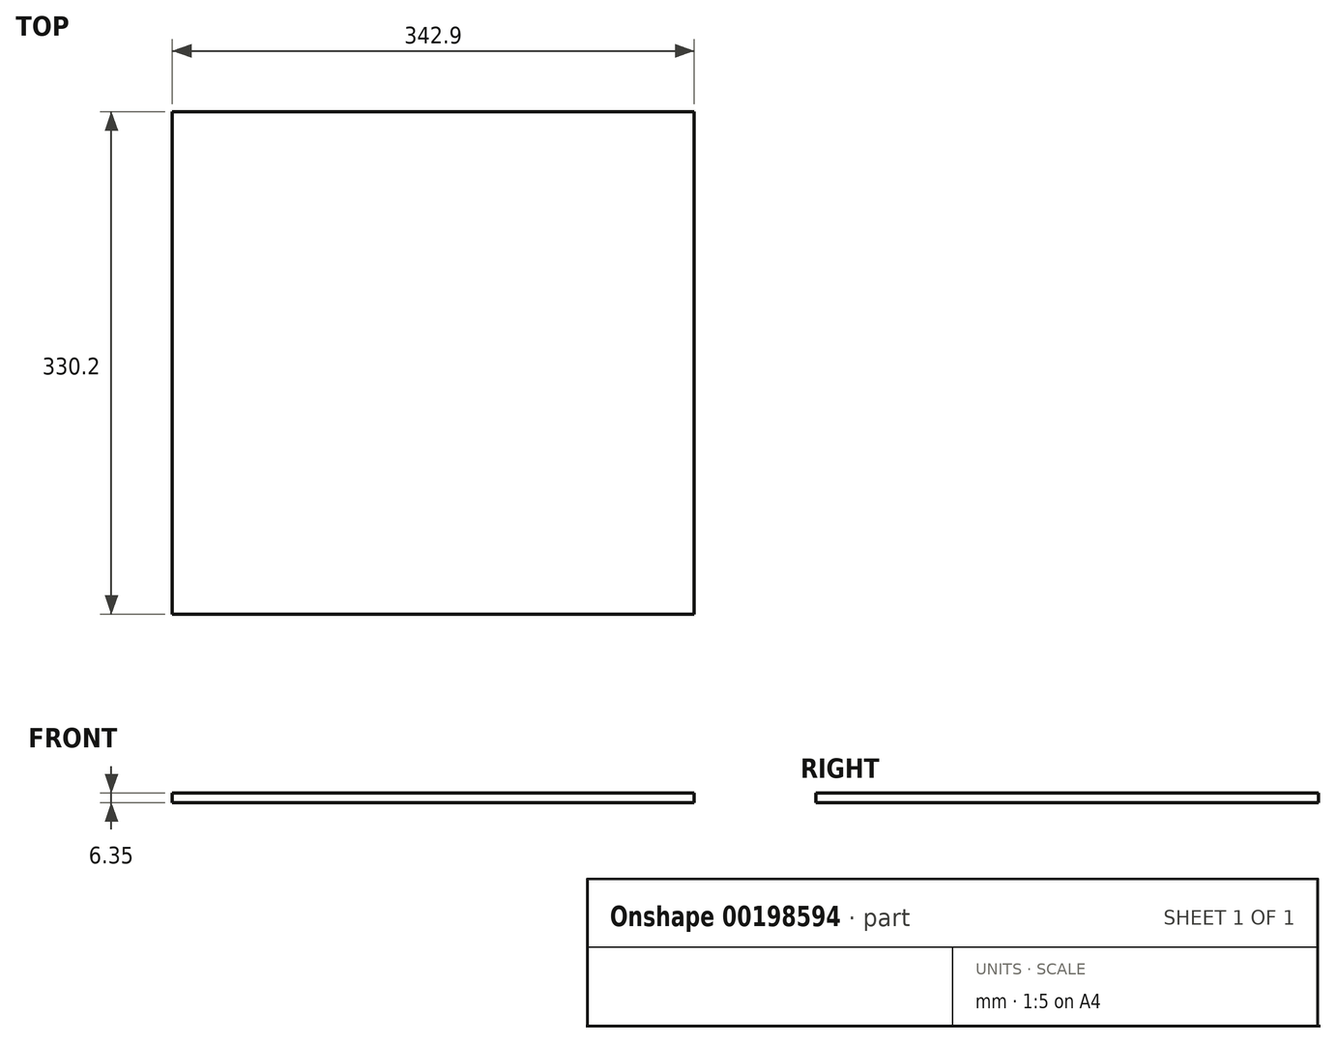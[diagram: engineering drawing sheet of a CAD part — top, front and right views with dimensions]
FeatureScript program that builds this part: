
annotation { "Feature Type Name" : "Feature", "Feature Type Description" : "" }
export const myFeature = defineFeature(function(context is Context, id is Id, definition is map)
    precondition{}
    {
        {
            var Q0;
            Q0=qCreatedBy(makeId("Top.planeOp"),FACE);
            var sketch = newSketch(context, id + "F0", { "sketchPlane" : qUnion([Q0])});
            skLineSegment(sketch, "E0.bottom", {"start": v(171.45, 165.1) * mm, "end": v(-171.45, 165.1) * mm});
            skLineSegment(sketch, "E0.top", {"start": v(171.45, -165.1) * mm, "end": v(-171.45, -165.1) * mm});
            skLineSegment(sketch, "E0.left", {"start": v(171.45, 165.1) * mm, "end": v(171.45, -165.1) * mm});
            skLineSegment(sketch, "E0.right", {"start": v(-171.45, 165.1) * mm, "end": v(-171.45, -165.1) * mm});
            skPoint(sketch, "E0.middle", {"position": v(0, 0) * mm});
            skSolve(sketch);
        }
        {
            var Q0;
            Q0 = qSketchRegion(id + "F0", true);
            extrude(context, id + "F1", {"entities" : qUnion([Q0]), "depth" : 6.35 * mm});
        }
    });
